# Revit family: Sanitary_Basins_Cosentino_Armony
name_source: partatom
category: Plumbing Fixtures
units: mm (PartAtom-declared; Revit-internal decimal feet)

## family parameters
Always vertical = Yes
Cut with Voids When Loaded = No
Host = Wall
Part Type = Normal
Room Calculation Point = No
Round Connector Dimension = Use Diameter
Shared = No

## types (1)
- Armony
    Assembly Code = D2010400
    CW Connection = No
    Default Elevation = 0 mm  [stored 0 ft]
    Description = The basin is one of the stars of your bathroom. Cosentino offers unique designs which fit smoothly into your room, your style, and the needs of your family.

Whether it’s for a master bathroom or a downstairs WC, we have the perfect product to transform your bathroom into a warm, welcoming space.
    Edition number = 1
    HW Connection = No
    Keynote = 10800
    Manufacturer = Cosentino
    Model = Armony
    Product Guid = 94ccfba4-6d37-4f0b-a6e1-04d45dce5c0f
    Product Material = Natural Stone - Cosentino - Silestone - Blanco Stellar - Suede
    Product data url = https://www.bimobject.com
    URL = www.cosentino.com
    Vent Connection = No

note: [stored X ft] marks values corroborated as IEEE doubles in the binary element streams (Revit-internal decimal feet)

## geometry (parser evidence)
native form markers: Sweep x3
no freeform markers — native parametric forms only
